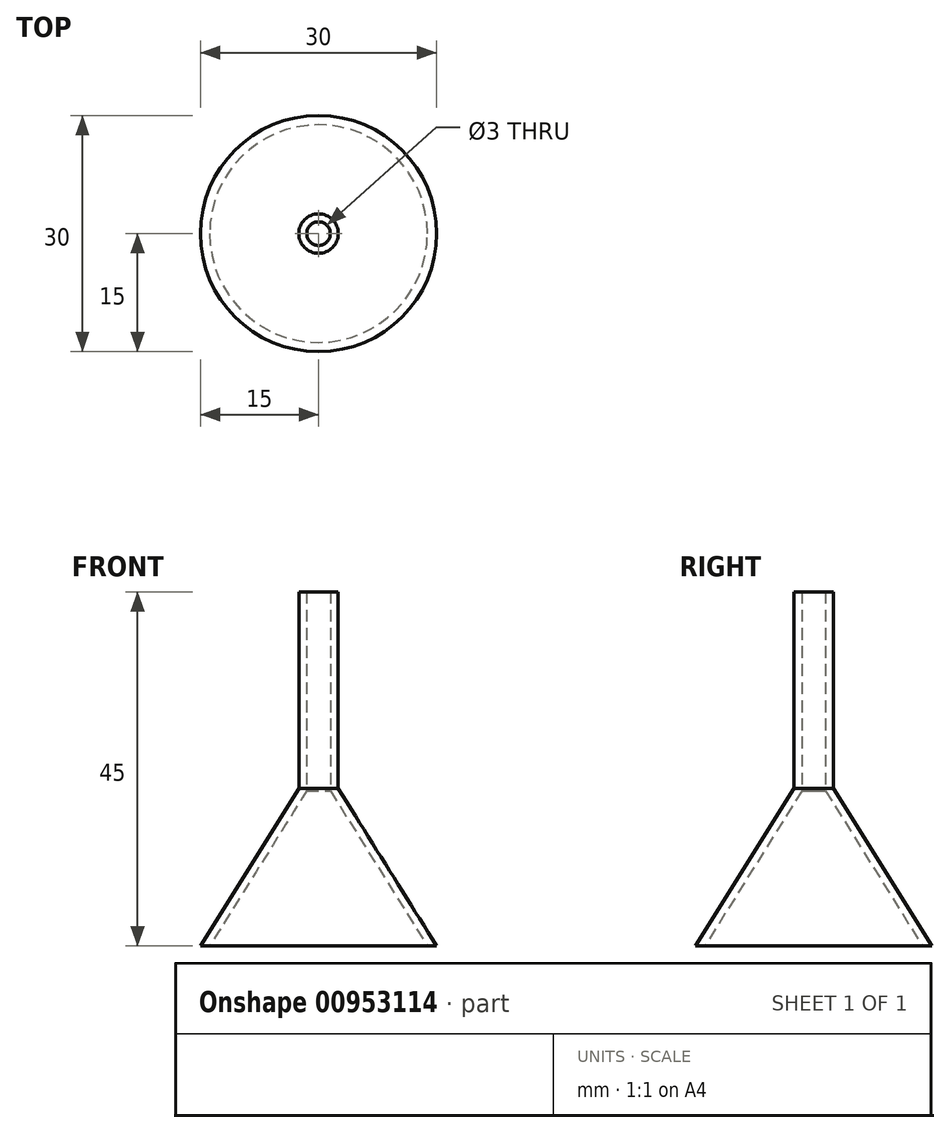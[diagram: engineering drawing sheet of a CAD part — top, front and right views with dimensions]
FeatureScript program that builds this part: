
annotation { "Feature Type Name" : "Feature", "Feature Type Description" : "" }
export const myFeature = defineFeature(function(context is Context, id is Id, definition is map)
    precondition{}
    {
        {
            var Q0;
            Q0=qCreatedBy(makeId("Top.planeOp"),FACE);
            var sketch = newSketch(context, id + "F0", { "sketchPlane" : qUnion([Q0])});
            skCircle(sketch, "E0", {"center": v(0, 0) * mm, "radius": 2.5 * mm});
            skSolve(sketch);
        }
        {
            var Q0;
            Q0=makeQuery(id+"F0.imprint","IMPRINT",FACE,{"disambiguationData":[TD([[makeQuery(id+"F0.imprint","IMPRINT",EDGE,{"derivedFrom":sQuery(id+"F0.wireOp",EDGE,"E0")}),1.0]])]});
            extrude(context, id + "F1", {"entities" : qUnion([Q0]), "depth" : 25 * mm, "offsetDistance" : 25 * mm});
        }
        {
            var Q0;
            Q0=qCreatedBy(makeId("Top.planeOp"),FACE);
            cPlane(context, id + "F2", {"entities" : qUnion([Q0]), "cplaneType" : CPlaneType.OFFSET, "offset" : 20 * mm, "oppositeDirection" : true, "width" : 150 * mm, "height" : 150 * mm});
        }
        {
            var Q0;
            Q0=qCreatedBy(id+"F2.planeOp",FACE);
            var sketch = newSketch(context, id + "F3", { "sketchPlane" : qUnion([Q0])});
            skCircle(sketch, "E1", {"center": v(0, 0) * mm, "radius": 15 * mm});
            skSolve(sketch);
        }
        {
            var Q1;
            Q1=makeQuery(id+"F3.imprint","IMPRINT",FACE,{"disambiguationData":[TD([[makeQuery(id+"F3.imprint","IMPRINT",EDGE,{"derivedFrom":sQuery(id+"F3.wireOp",EDGE,"E1")}),1.0]])]});
            var Q2;
            Q2=makeQuery(id+"F0.imprint","IMPRINT",FACE,{"disambiguationData":[TD([[makeQuery(id+"F0.imprint","IMPRINT",EDGE,{"derivedFrom":sQuery(id+"F0.wireOp",EDGE,"E0")}),1.0]])]});
            loft(context, id + "F4", {"operationType" : NewBodyOperationType.ADD, "sheetProfilesArray" : [{ "sheetProfileEntities" : qUnion([Q1]) }, { "sheetProfileEntities" : qUnion([Q2]) }]});
        }
        {
            var Q0;
            Q0=makeQuery(id+"F1.opExtrude","CAP_FACE",FACE,{"disambiguationData":[OSD([sQuery(id+"F0.wireOp",EDGE,"E0")])],"isStart":false});
            var Q1;
            Q1=makeQuery(id+"F4.opLoft","CAP_FACE",FACE,{"disambiguationData":[OSD([makeQuery(id+"F3.imprint","IMPRINT",FACE,{"disambiguationData":[TD([[makeQuery(id+"F3.imprint","IMPRINT",EDGE,{"derivedFrom":sQuery(id+"F3.wireOp",EDGE,"E1")}),1.0]])]})])],"isStart":true});
            shell(context, id + "F5", {"entities" : qUnion([Q0, Q1]), "thickness" : 1 * mm});
        }
    });
